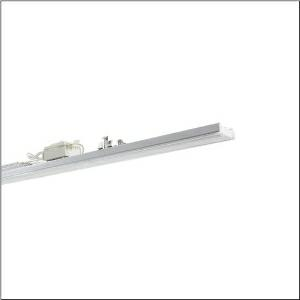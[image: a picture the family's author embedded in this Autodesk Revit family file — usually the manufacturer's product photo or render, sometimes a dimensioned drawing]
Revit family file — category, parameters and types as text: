
# Revit family: licross_r__11_recessed_mo_51tl19mn495g_cade
name_source: partatom
category: Lighting Fixtures
units: mm (PartAtom-declared; Revit-internal decimal feet)

## family parameters
Cut with Voids When Loaded = No
Host = Face
Light Source = No
Part Type = Normal
Room Calculation Point = No
Round Connector Dimension = Use Diameter
Shared = No

## types (1)
- --- (1 x LED, 9850 lm, 55.2 W, 4000K)
    Apparent Load = 55 VA
    CIE Flux Codes = 55 90 98 100 100
    Color Rendering = 80
    Color Temperature = 4000K
    Default Elevation = 1800 mm
    Description = Licross® 11 Recessed MO, luminaire insert, of sheet steel, coil coated, white, length: 1.500mm, width: 66mm, height: 67mm, LED rated luminous flux: 9.860lm, light colour: 840, control gear: ON/OFF Multilumen, with plug, 3-pole, with phase selection, mains connection: 220..240V, AC, 50/60Hz, rated input power: 55W, internal wiring halogen-free, primary light control with lens, of plastic, primary optical cover: cover, of PMMA, light emission: direct distribution, primary light characteristic: double asymmetric, protection rating (complete): IP40, insulation class (complete): insulation class I (protective earthing), certification: CE, ENEC, VDE, UKCA, protection symbol: D if used in an environment without relevant dust loads with corresponding accessories, impact resistance: IK06, permissible ambient temperature for indoor applications: -35..+40°C, corresponds to IFS (International Featured Standards) requirements for safety and quality in the food industry, reducing of maximum allowable ambient temperature of 5°C with ceiling mounting, packaging unit: 1 piece
    Height = 58 mm
    Lamp = 1 x LED
    Lamp Light Flux = 9850 lm
    Lamp Power = 55.2 W
    Lamp count = 1
    Length = 1500 mm
    Luminous efficacy = 178 lm/W
    Manufacturer = Siteco
    ModVariant = No
    Model = 51TL19MN495G
    Mounting Place = Ceiling
    Mounting Type = Pendant
    Number of Poles = 1
    OnlyDefault = Yes
    Power Factor = 1
    Product Name = Licross® 11 Recessed MO
    Product group = luminaire insert | ceiling pendant
    ProductGroupID = 902
    Protection Class = Protection class I
    Protection Degree = IP 40
    RLX_Detail_Level = 1
    RLX_Emergency_Light_Flux = 0 lm
    RLX_Emergency_Type = 0
    RLX_Emergency_Type_DB = No
    RlxData = <blob elided: 22209 chars, md5=3a581866>
    Socket = socket
    Standby Power = 0 W
    System Light Flux = 9850 lm
    System Power = 55 W
    Type Comments = factory setting: luminous flux: 100 % | (A | C | E) | 126 mA
    Type Image = l_1296930.jpg
    URL = http://relux.com
    VarID = @adj_107177
    Voltage = 0 V
    Weight = 0.00 kg
    Width = 66 mm

## geometry (parser evidence)
native form markers: Blend x4, Sweep x12
no freeform markers — native parametric forms only
